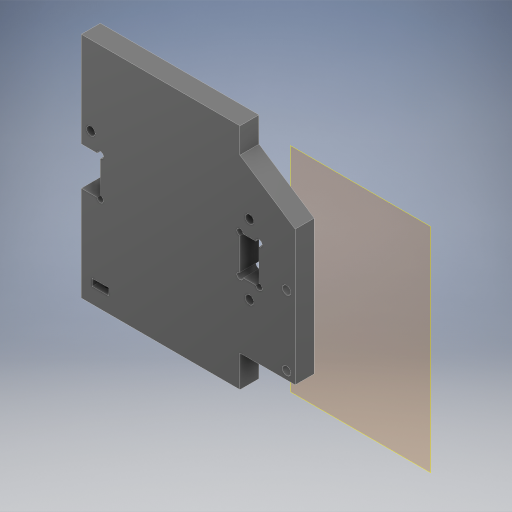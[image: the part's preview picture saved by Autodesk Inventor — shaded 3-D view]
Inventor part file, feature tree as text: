
AUTODESK INVENTOR PART (.ipt)
format: ipt  version: 2024 (Build 280153000, 153)  size: 382,464 bytes
history: native  units: in
note: dims shown in document units (in); Inventor stores cm internally (conversion verified against a paired STEP export)
features: extrude x8, sketch x8, other x5, projected_geometry x3, reference x1
ambient origin geometry x8: Origin, YZ Plane, XZ Plane, XY Plane, X Axis, Y Axis, Z Axis, Center Point
bodies: Body1 (feature_tree)
feature tree (25):
  other  "솔리드1"
  other  "작업 평면1"
  extrude  "돌출1"  Depth=0.0039in
  extrude  "돌출2"  Depth=0.1063in
  extrude  "돌출3"  Depth=0.1063in
  extrude  "돌출4"  Depth=0.1063in
  extrude  "돌출5"  Depth=0.4724in
  extrude  "돌출6"  Depth=0.1063in
  extrude  "돌출7"  Depth=0.1063in
  extrude  "돌출8"  Depth=0.2362in TaperAngle=0.0deg
  sketch  "스케치1"
  reference  "참조1"
  sketch  "스케치2"
  sketch  "스케치3"
  projected_geometry  "투영된 루프1"
  sketch  "스케치5"
  sketch  "스케치6"
  sketch  "스케치7"
  projected_geometry  "투영된 루프2"
  sketch  "스케치8"
  projected_geometry  "투영된 루프3"
  sketch  "스케치9"
  other  "조립품9"
  other  "MX-64T+idle.ipt:2"
  other  "MX-64T:1"
